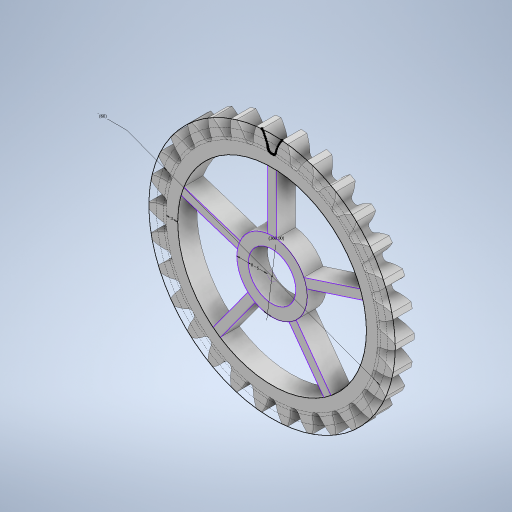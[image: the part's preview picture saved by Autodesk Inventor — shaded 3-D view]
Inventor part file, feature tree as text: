
AUTODESK INVENTOR PART (.ipt)
format: ipt  version: 2023 (Build 270158000, 158)  size: 518,656 bytes
history: native  units: mm
features: extrude x3, pattern_circular x1
ambient origin geometry x8: Origin, YZ Plane, XZ Plane, XY Plane, X Axis, Y Axis, Z Axis, Center Point
bodies: Solid1 (feature_tree)
feature tree (4):
  extrude  "Extrusion1"  Depth=5.0mm
  extrude  "Extrusion2"  TaperAngle=0.0deg  [1 undecoded]
  extrude  "Extrusion3"  Depth=3.0mm
  pattern_circular  "Circular Pattern1"  [2 undecoded]
note: 3 required parameter values undecoded (feature->parameter linkage not recoverable at this tier; creation-order binding heuristic only, values carry confidence <= 0.55)
